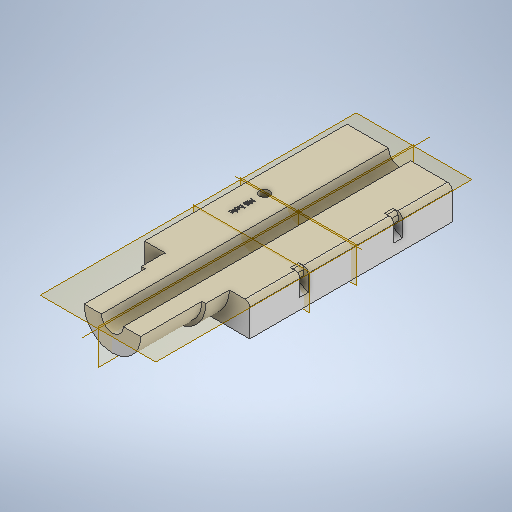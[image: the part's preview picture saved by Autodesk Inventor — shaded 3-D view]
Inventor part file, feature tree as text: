
AUTODESK INVENTOR PART (.ipt)
format: ipt  version: 2025 (Build 290162000, 162)  size: 500,736 bytes
history: native  units: mm
features: sketch x7, extrude x5, plane x1, mirror x1, fillet x1, hole x1, emboss x1
ambient origin geometry x8: Origin, YZ Plane, XZ Plane, XY Plane, X Axis, Y Axis, Z Axis, Center Point
bodies: Solid1 (feature_tree)
feature tree (17):
  extrude  "Extrusion1"  Depth=129.0mm
  extrude  "Extrusion2"  Depth=20.5mm
  extrude  "Extrusion3"  Depth=15.0mm TaperAngle=0.0deg
  extrude  "Extrusion4"  TaperAngle=180.0deg  [1 undecoded]
  plane  "Work Plane1"
  extrude  "Extrusion5"  Depth=7.0mm
  mirror  "Mirror1"
  fillet  "Fillet1"  [1 undecoded]
  hole  "Hole1"  [1 undecoded]
  emboss  "Emboss1"
  sketch  "Sketch1"  dims[d0=20.5mm d1=129.0mm]
  sketch  "Sketch2"  dims[d2=67.0mm d3=0.0mm d4=20.5mm]
  sketch  "Sketch3"  dims[d5=180.0deg d6=15.0mm d7=0.0mm]
  sketch  "Sketch4"  dims[d8=18.0mm d9=180.0deg]
  sketch  "Sketch5"  dims[d10=39.0mm d11=0.0mm d12=7.0mm d13=180.0deg]
  sketch  "Sketch6"  dims[d14=0.0mm d15=0.0mm d16=30.0mm]
  sketch  "Sketch7"  dims[d17=2.0mm d18=1.5mm d19=1.0mm d20=5.4mm d21=0.0mm d22=3.0mm d23=6.2mm d24=6.0mm d25=10.5mm d26=6.0mm d27=90.0deg d28=10.0mm d29=0.0mm d30=12.0mm d31=1.0mm d32=0.0mm]
note: 3 required parameter values undecoded (feature->parameter linkage not recoverable at this tier; creation-order binding heuristic only, values carry confidence <= 0.55)
